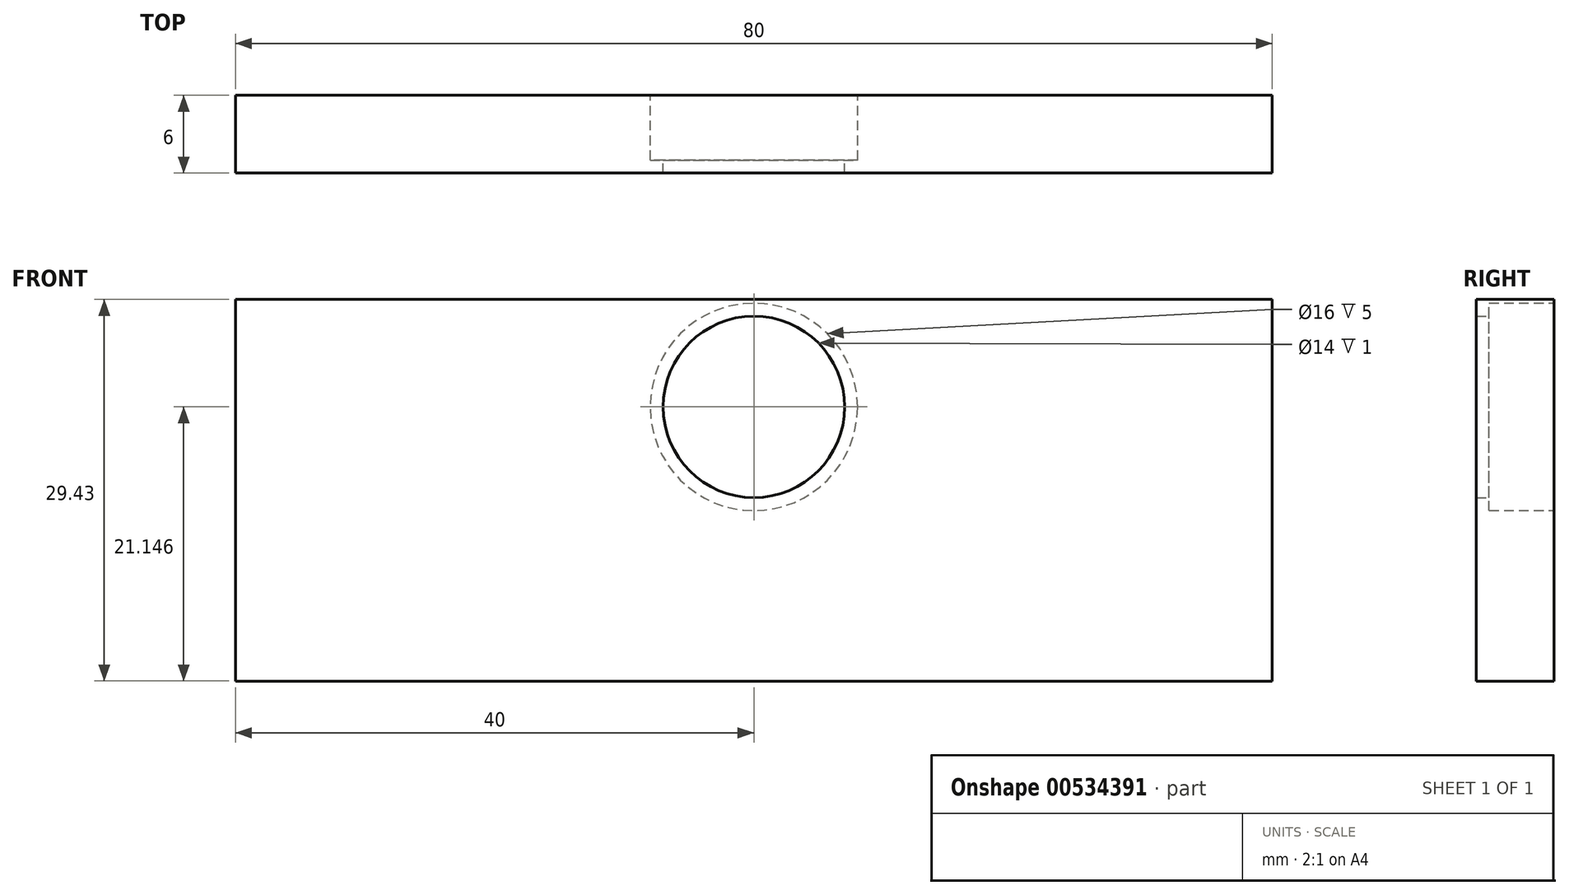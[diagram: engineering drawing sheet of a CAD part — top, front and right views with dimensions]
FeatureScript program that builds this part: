
annotation { "Feature Type Name" : "Feature", "Feature Type Description" : "" }
export const myFeature = defineFeature(function(context is Context, id is Id, definition is map)
    precondition{}
    {
        {
            var Q0;
            Q0=qCreatedBy(makeId("Front.planeOp"),FACE);
            var sketch = newSketch(context, id + "F0", { "sketchPlane" : qUnion([Q0])});
            skLineSegment(sketch, "E0", {"start": v(0, 0) * mm, "end": v(-40, 0) * mm});
            skLineSegment(sketch, "E1", {"start": v(0, 0) * mm, "end": v(40, 0) * mm});
            skLineSegment(sketch, "E2", {"start": v(0, 0) * mm, "end": v(0, -8.28) * mm, "construction": true});
            skLineSegment(sketch, "E3", {"start": v(0, -8.28) * mm, "end": v(0, -29.43) * mm, "construction": true});
            skLineSegment(sketch, "E4", {"start": v(40, 0) * mm, "end": v(40, -29.43) * mm});
            skLineSegment(sketch, "E5", {"start": v(0, -29.43) * mm, "end": v(40, -29.43) * mm});
            skLineSegment(sketch, "E6", {"start": v(-40, 0) * mm, "end": v(-40, -29.43) * mm});
            skLineSegment(sketch, "E7", {"start": v(-40, -29.43) * mm, "end": v(0, -29.43) * mm});
            skSolve(sketch);
        }
        {
            var Q0;
            Q0=makeQuery(id+"F0.imprint","IMPRINT",FACE,{"disambiguationData":[TD([[makeQuery(id+"F0.imprint","IMPRINT",EDGE,{"derivedFrom":sQuery(id+"F0.wireOp",EDGE,"E0")}),1.0]])]});
            extrude(context, id + "F1", {"entities" : qUnion([Q0]), "depth" : 6 * mm, "offsetDistance" : 25 * mm});
        }
        {
            var Q0;
            Q0=makeQuery(id+"F0.imprint","IMPRINT",FACE,{"disambiguationData":[TD([[makeQuery(id+"F0.imprint","IMPRINT",EDGE,{"derivedFrom":sQuery(id+"F0.wireOp",EDGE,"E0")}),1.0]])]});
            var sketch = newSketch(context, id + "F2", { "sketchPlane" : qUnion([Q0])});
            skLineSegment(sketch, "E8", {"start": v(0, 0) * mm, "end": v(0, -8.28) * mm, "construction": true});
            skCircle(sketch, "E9", {"center": v(0, -8.28) * mm, "radius": 8 * mm});
            skCircle(sketch, "E10", {"center": v(0, -8.28) * mm, "radius": 7 * mm});
            skSolve(sketch);
        }
        {
            var Q0;
            Q0=makeQuery(id+"F2.imprint","IMPRINT",FACE,{"disambiguationData":[TD([[makeQuery(id+"F2.imprint","IMPRINT",EDGE,{"derivedFrom":sQuery(id+"F2.wireOp",EDGE,"E9")}),1.0]])]});
            var Q1;
            Q1=sQuery(id+"F2.wireOp",EDGE,"E9");
            extrude(context, id + "F3", {"entities" : qUnion([Q0]), "operationType" : NewBodyOperationType.REMOVE, "surfaceEntities" : qUnion([Q1]), "depth" : 5 * mm, "offsetDistance" : 25 * mm});
        }
        {
            var Q0;
            Q0=makeQuery(id+"F2.imprint","IMPRINT",FACE,{"disambiguationData":[TD([[makeQuery(id+"F2.imprint","IMPRINT",EDGE,{"derivedFrom":sQuery(id+"F2.wireOp",EDGE,"E10")}),1.0]])]});
            var Q1;
            Q1=sQuery(id+"F2.wireOp",EDGE,"E10");
            extrude(context, id + "F4", {"entities" : qUnion([Q0]), "operationType" : NewBodyOperationType.REMOVE, "surfaceEntities" : qUnion([Q1]), "depth" : 26.3 * mm, "offsetDistance" : 25 * mm});
        }
    });
